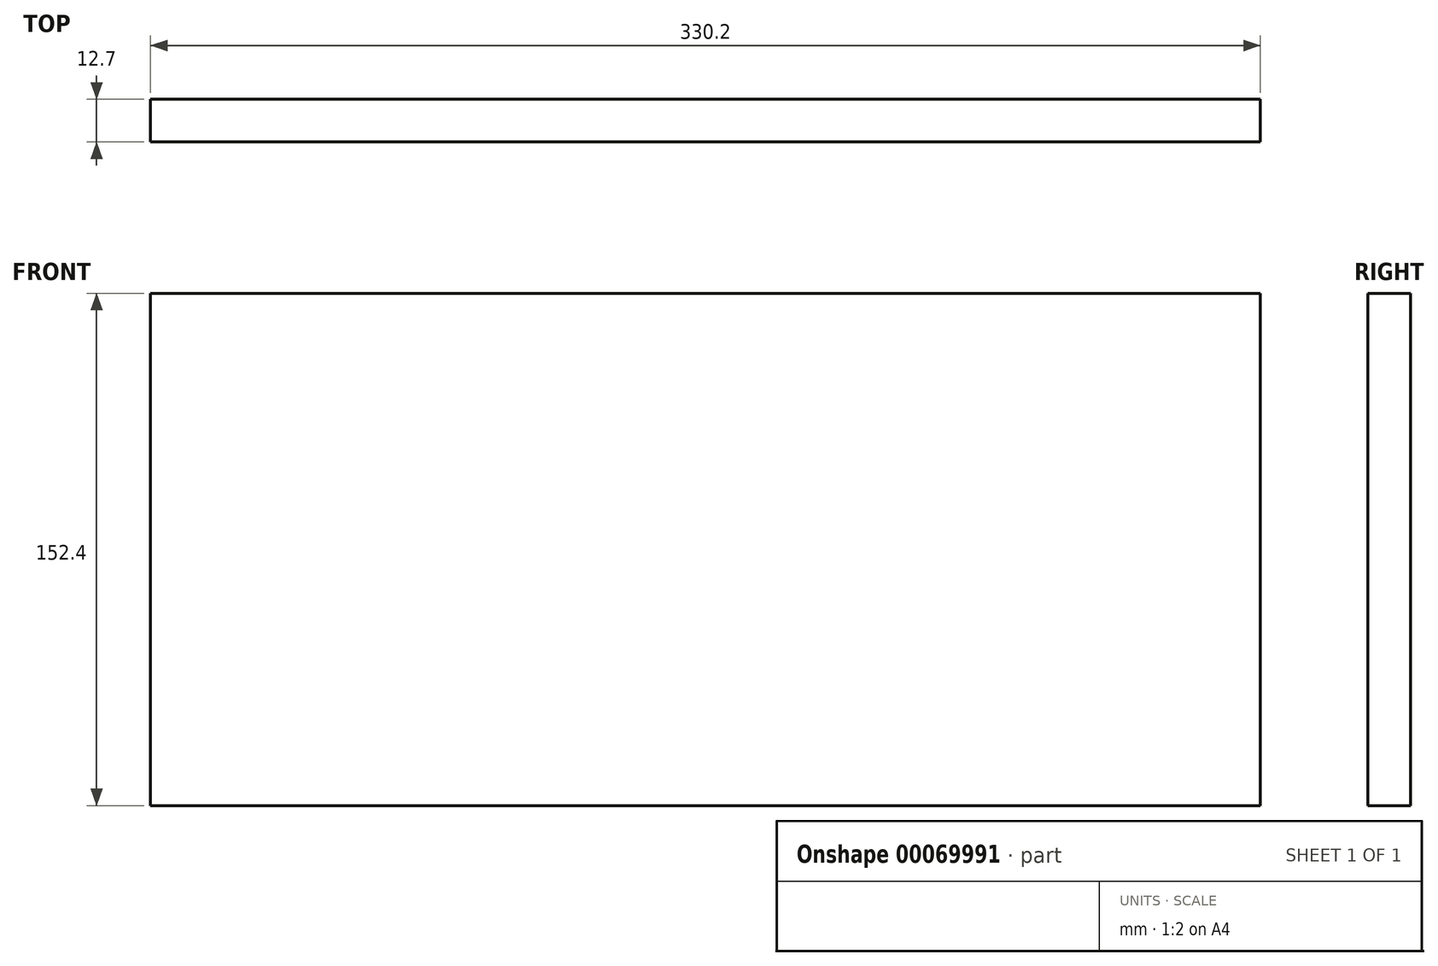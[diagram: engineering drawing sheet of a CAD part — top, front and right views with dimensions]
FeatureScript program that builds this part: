
annotation { "Feature Type Name" : "Feature", "Feature Type Description" : "" }
export const myFeature = defineFeature(function(context is Context, id is Id, definition is map)
    precondition{}
    {
        {
            var Q0;
            Q0=qCreatedBy(makeId("Front.planeOp"),FACE);
            var sketch = newSketch(context, id + "F0", { "sketchPlane" : qUnion([Q0])});
            skLineSegment(sketch, "E0.rect.bottom", {"start": v(165.1, 76.2) * mm, "end": v(-165.1, 76.2) * mm});
            skLineSegment(sketch, "E0.rect.top", {"start": v(165.1, -76.2) * mm, "end": v(-165.1, -76.2) * mm});
            skLineSegment(sketch, "E0.rect.left", {"start": v(165.1, 76.2) * mm, "end": v(165.1, -76.2) * mm});
            skLineSegment(sketch, "E0.rect.right", {"start": v(-165.1, 76.2) * mm, "end": v(-165.1, -76.2) * mm});
            skPoint(sketch, "E0.rect.middle", {"position": v(0, 0) * mm});
            skSolve(sketch);
        }
        {
            var Q0;
            Q0=makeQuery(id+"F0.imprint","IMPRINT",FACE,{"disambiguationData":[TD([[makeQuery(id+"F0.imprint","IMPRINT",EDGE,{"derivedFrom":sQuery(id+"F0.wireOp",EDGE,"E0.rect.bottom")}),1.0]])]});
            extrude(context, id + "F1", {"entities" : qUnion([Q0]), "depth" : 12.7 * mm});
        }
    });
